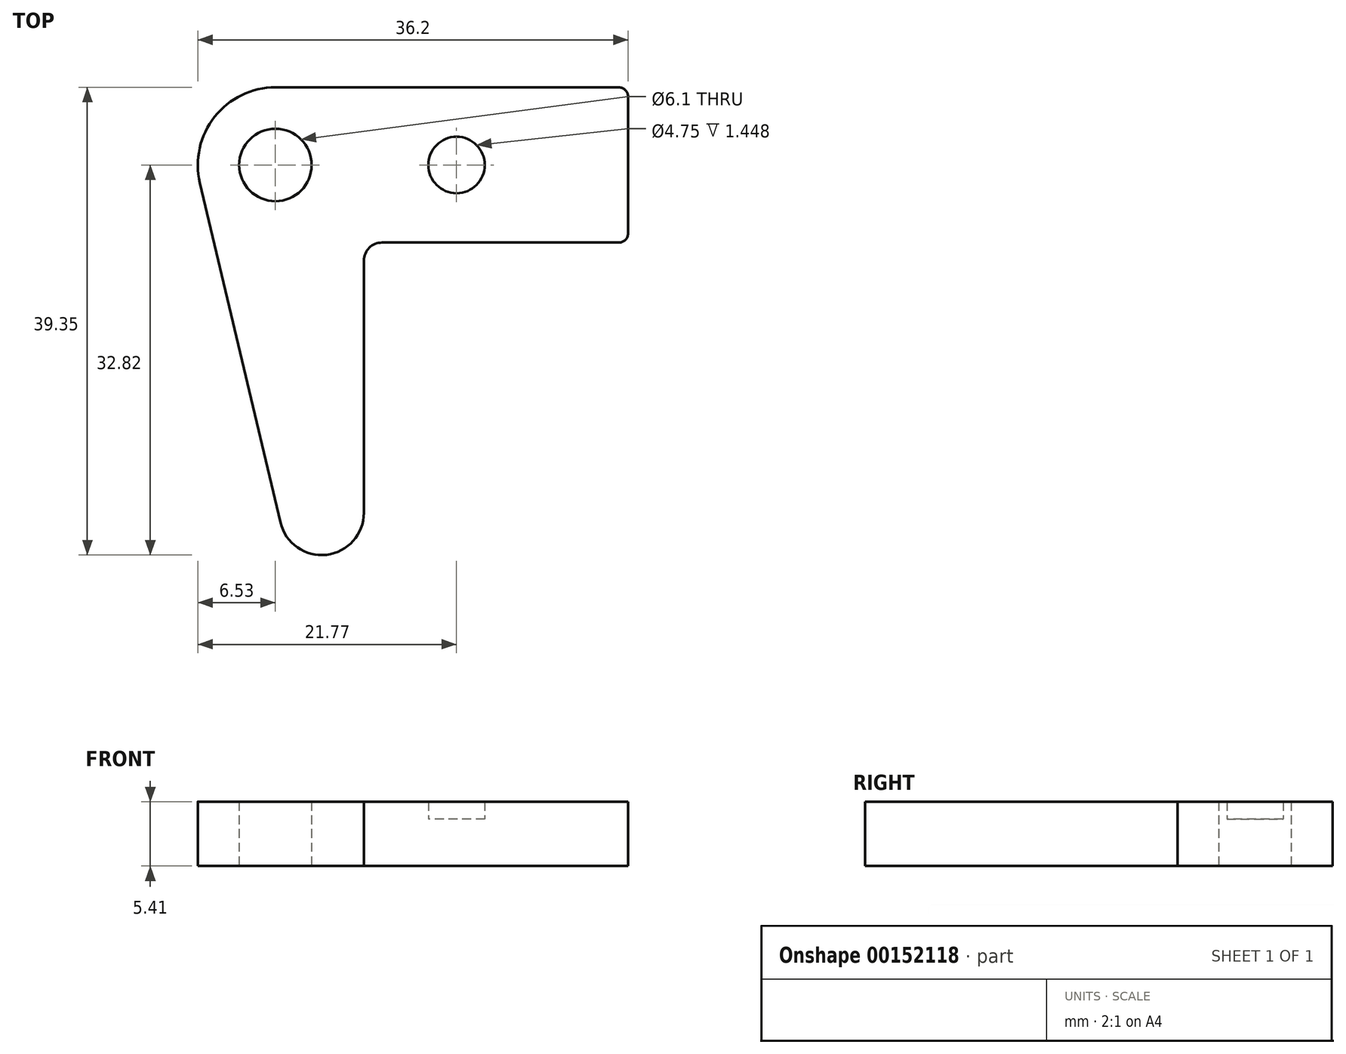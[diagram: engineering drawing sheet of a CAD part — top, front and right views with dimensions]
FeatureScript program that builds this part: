
annotation { "Feature Type Name" : "Feature", "Feature Type Description" : "" }
export const myFeature = defineFeature(function(context is Context, id is Id, definition is map)
    precondition{}
    {
        {
            var Q0;
            Q0=qCreatedBy(makeId("Top.planeOp"),FACE);
            var sketch = newSketch(context, id + "F0", { "sketchPlane" : qUnion([Q0])});
            skCircle(sketch, "E0", {"center": v(0, 0) * mm, "radius": 3.05 * mm});
            skLineSegment(sketch, "E1", {"start": v(0, 6.53) * mm, "end": v(28.9, 6.53) * mm});
            skArc(sketch, "E2", {"start": v(0, 6.53) * mm, "mid": v(-5.12, 4.05) * mm, "end": v(-6.35, -1.5) * mm});
            skLineSegment(sketch, "E3.0", {"start": v(29.67, 5.77) * mm, "end": v(29.67, -5.77) * mm});
            skLineSegment(sketch, "E4", {"start": v(8.97, -6.53) * mm, "end": v(28.9, -6.53) * mm});
            skLineSegment(sketch, "E5", {"start": v(7.44, -8.05) * mm, "end": v(7.44, -29.26) * mm});
            skArc(sketch, "E6", {"start": v(0.43, -30.08) * mm, "mid": v(4.3, -32.8) * mm, "end": v(7.44, -29.26) * mm});
            skLineSegment(sketch, "E7", {"start": v(-6.35, -1.5) * mm, "end": v(0.43, -30.08) * mm});
            skPoint(sketch, "E8.orphan", {"position": v(0, -28.28) * mm});
            skPoint(sketch, "E9.visualSharp", {"position": v(7.44, -6.53) * mm});
            skArc(sketch, "E9.filletArc", {"start": v(8.97, -6.53) * mm, "mid": v(7.89, -6.97) * mm, "end": v(7.44, -8.05) * mm});
            skPoint(sketch, "E10.visualSharp", {"position": v(29.67, 6.53) * mm});
            skArc(sketch, "E10.filletArc", {"start": v(29.67, 5.77) * mm, "mid": v(29.44, 6.3) * mm, "end": v(28.9, 6.53) * mm});
            skPoint(sketch, "E11.visualSharp", {"position": v(29.67, -6.53) * mm});
            skArc(sketch, "E11.filletArc", {"start": v(28.9, -6.53) * mm, "mid": v(29.44, -6.3) * mm, "end": v(29.67, -5.77) * mm});
            skCircle(sketch, "E12", {"center": v(15.24, 0) * mm, "radius": 2.37 * mm});
            skSolve(sketch);
        }
        {
            var Q0;
            Q0=makeQuery(id+"F0.imprint","IMPRINT",FACE,{"disambiguationData":[TD([[makeQuery(id+"F0.imprint","IMPRINT",EDGE,{"derivedFrom":sQuery(id+"F0.wireOp",EDGE,"E0")}),-1.0]])]});
            var Q1;
            Q1=makeQuery(id+"F0.imprint","IMPRINT",FACE,{"disambiguationData":[TD([[makeQuery(id+"F0.imprint","IMPRINT",EDGE,{"derivedFrom":sQuery(id+"F0.wireOp",EDGE,"E12")}),1.0]])]});
            extrude(context, id + "F1", {"entities" : qUnion([Q0, Q1]), "depth" : 5.4 * mm});
        }
        {
            var Q0;
            Q0=makeQuery(id+"F0.imprint","IMPRINT",FACE,{"disambiguationData":[TD([[makeQuery(id+"F0.imprint","IMPRINT",EDGE,{"derivedFrom":sQuery(id+"F0.wireOp",EDGE,"E12")}),1.0]])]});
            extrude(context, id + "F2", {"entities" : qUnion([Q0]), "operationType" : NewBodyOperationType.REMOVE, "depth" : 25.4 * mm, "hasSecondDirection" : true, "secondDirectionOppositeDirection" : false, "secondDirectionDepth" : 3.96 * mm});
        }
    });
